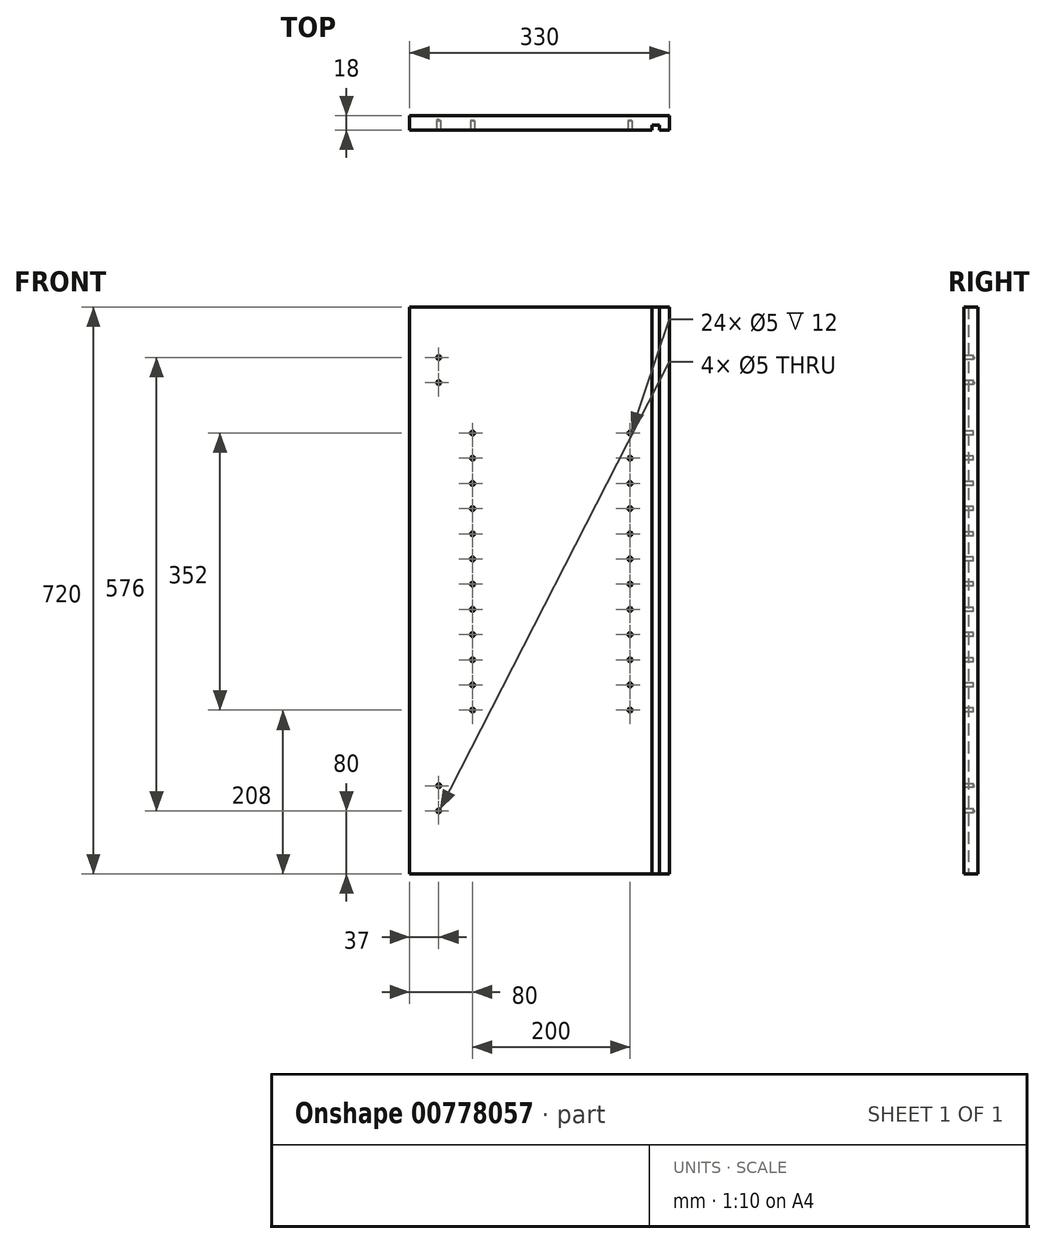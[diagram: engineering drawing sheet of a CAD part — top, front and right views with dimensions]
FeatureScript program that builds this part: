
annotation { "Feature Type Name" : "Feature", "Feature Type Description" : "" }
export const myFeature = defineFeature(function(context is Context, id is Id, definition is map)
    precondition{}
    {
        {
            var Q0;
            Q0=qCreatedBy(makeId("Front.planeOp"),FACE);
            var sketch = newSketch(context, id + "F0", { "sketchPlane" : qUnion([Q0])});
            skLineSegment(sketch, "E0.bottom", {"start": v(243.8, -214.98) * mm, "end": v(305.16, -214.98) * mm});
            skLineSegment(sketch, "E0.top", {"start": v(243.8, -338.54) * mm, "end": v(305.16, -338.54) * mm});
            skLineSegment(sketch, "E0.left", {"start": v(243.8, -214.98) * mm, "end": v(243.8, -338.54) * mm});
            skLineSegment(sketch, "E0.right", {"start": v(305.16, -214.98) * mm, "end": v(305.16, -338.54) * mm});
            skLineSegment(sketch, "E1.bottom", {"start": v(-330, 720) * mm, "end": v(0, 720) * mm});
            skLineSegment(sketch, "E1.top", {"start": v(-330, 0) * mm, "end": v(0, 0) * mm});
            skLineSegment(sketch, "E1.left", {"start": v(-330, 720) * mm, "end": v(-330, 0) * mm});
            skLineSegment(sketch, "E1.right", {"start": v(0, 720) * mm, "end": v(0, 0) * mm});
            skSolve(sketch);
        }
        {
            var Q0;
            Q0=makeQuery(id+"F0.imprint","IMPRINT",FACE,{"disambiguationData":[TD([[makeQuery(id+"F0.imprint","IMPRINT",EDGE,{"derivedFrom":sQuery(id+"F0.wireOp",EDGE,"E1.bottom")}),-1.0]])]});
            extrude(context, id + "F1", {"entities" : qUnion([Q0]), "depth" : 18 * mm, "offsetDistance" : 25 * mm});
        }
        {
            var Q0;
            Q0=makeQuery(id+"F1.opExtrude","CAP_FACE",FACE,{"disambiguationData":[OSD([sQuery(id+"F0.wireOp",EDGE,"E1.bottom"),sQuery(id+"F0.wireOp",EDGE,"E1.top"),sQuery(id+"F0.wireOp",EDGE,"E1.left"),sQuery(id+"F0.wireOp",EDGE,"E1.right")])],"isStart":false});
            var sketch = newSketch(context, id + "F2", { "sketchPlane" : qUnion([Q0])});
            skLineSegment(sketch, "E2", {"start": v(-293, 0) * mm, "end": v(-293, 720) * mm, "construction": true});
            skCircle(sketch, "E3", {"center": v(-293, 656) * mm, "radius": 2.5 * mm});
            skCircle(sketch, "E4", {"center": v(-293, 624) * mm, "radius": 2.5 * mm});
            skCircle(sketch, "E5", {"center": v(-293, 80) * mm, "radius": 2.5 * mm});
            skCircle(sketch, "E6", {"center": v(-293, 112) * mm, "radius": 2.5 * mm});
            skSolve(sketch);
        }
        {
            var Q0;
            Q0=sQuery(id+"F2.wireOp",VERTEX,"E3.center");
            var Q1;
            Q1=sQuery(id+"F2.wireOp",VERTEX,"E4.center");
            var Q2;
            Q2=sQuery(id+"F2.wireOp",VERTEX,"E6.center");
            var Q3;
            Q3=sQuery(id+"F2.wireOp",VERTEX,"E5.center");
            var Q4;
            Q4=makeQuery(id+"F1.opExtrude","SWEPT_BODY",BODY,{"disambiguationData":[OSD([sQuery(id+"F0.wireOp",EDGE,"E1.bottom"),sQuery(id+"F0.wireOp",EDGE,"E1.top"),sQuery(id+"F0.wireOp",EDGE,"E1.left"),sQuery(id+"F0.wireOp",EDGE,"E1.right")])]});
            hole(context, id + "F3", {"style" : HoleStyle.SIMPLE, "endStyle" : HoleEndStyle.BLIND, "holeDiameter" : 5 * mm, "majorDiameter" : 5 * mm, "holeDepth" : 12 * mm, "isTappedThrough" : true, "tappedDepth" : 12 * mm, "tapClearance" : 3, "locations" : qUnion([Q0, Q1, Q2, Q3]), "scope" : qUnion([Q4])});
        }
        {
            var Q0;
            Q0=makeQuery(id+"F1.opExtrude","CAP_FACE",FACE,{"disambiguationData":[OSD([sQuery(id+"F0.wireOp",EDGE,"E1.bottom"),sQuery(id+"F0.wireOp",EDGE,"E1.top"),sQuery(id+"F0.wireOp",EDGE,"E1.left"),sQuery(id+"F0.wireOp",EDGE,"E1.right")])],"isStart":false});
            var sketch = newSketch(context, id + "F4", { "sketchPlane" : qUnion([Q0])});
            skLineSegment(sketch, "E7", {"start": v(-12.5, 720) * mm, "end": v(-12.5, 0) * mm});
            skLineSegment(sketch, "E8", {"start": v(-22, 720) * mm, "end": v(-22, 0) * mm});
            skSolve(sketch);
        }
        {
            var Q0;
            {var subQ0=sQuery(id+"F4.wireOp",EDGE,"E7");Q0=makeQuery(id+"F4.imprint","IMPRINT",FACE,{"disambiguationData":[TD([[makeQuery(id+"F4.imprint","IMPRINT",EDGE,{"derivedFrom":subQ0}),-1.0]])]});}
            extrude(context, id + "F5", {"entities" : qUnion([Q0]), "operationType" : NewBodyOperationType.REMOVE, "oppositeDirection" : true, "depth" : 6 * mm, "offsetDistance" : 25 * mm});
        }
        {
            var Q0;
            {var subQ0=sQuery(id+"F0.wireOp",EDGE,"E1.top");var subQ1=sQuery(id+"F0.wireOp",EDGE,"E1.left");var subQ2=sQuery(id+"F0.wireOp",EDGE,"E1.bottom");Q0=makeQuery(id+"F5.boolean.opBoolean","SPLIT",FACE,{"disambiguationData":[TD([makeQuery(id+"F1.opExtrude","SWEPT_FACE",FACE,{"disambiguationData":[OSD([subQ1])]})])],"derivedFrom":makeQuery(id+"F1.opExtrude","CAP_FACE",FACE,{"disambiguationData":[OSD([subQ2,subQ0,subQ1,sQuery(id+"F0.wireOp",EDGE,"E1.right")])],"isStart":false})});}
            var sketch = newSketch(context, id + "F6", { "sketchPlane" : qUnion([Q0])});
            skLineSegment(sketch, "E9", {"start": v(-250, 720) * mm, "end": v(-250, 0) * mm, "construction": true});
            skLineSegment(sketch, "E10", {"start": v(-50, 720) * mm, "end": v(-50, 0) * mm, "construction": true});
            skCircle(sketch, "E11", {"center": v(-250, 208) * mm, "radius": 2.5 * mm});
            skCircle(sketch, "E12.0.1.0", {"center": v(-250, 240) * mm, "radius": 2.5 * mm});
            skCircle(sketch, "E12.0.2.0", {"center": v(-250, 272) * mm, "radius": 2.5 * mm});
            skCircle(sketch, "E12.0.3.0", {"center": v(-250, 304) * mm, "radius": 2.5 * mm});
            skCircle(sketch, "E12.0.4.0", {"center": v(-250, 336) * mm, "radius": 2.5 * mm});
            skCircle(sketch, "E12.0.5.0", {"center": v(-250, 368) * mm, "radius": 2.5 * mm});
            skCircle(sketch, "E12.0.6.0", {"center": v(-250, 400) * mm, "radius": 2.5 * mm});
            skCircle(sketch, "E12.0.7.0", {"center": v(-250, 432) * mm, "radius": 2.5 * mm});
            skCircle(sketch, "E12.0.8.0", {"center": v(-250, 464) * mm, "radius": 2.5 * mm});
            skCircle(sketch, "E12.0.9.0", {"center": v(-250, 496) * mm, "radius": 2.5 * mm});
            skCircle(sketch, "E12.0.10.0", {"center": v(-250, 528) * mm, "radius": 2.5 * mm});
            skCircle(sketch, "E12.0.11.0", {"center": v(-250, 560) * mm, "radius": 2.5 * mm});
            skCircle(sketch, "E12.1.1.0", {"center": v(-250, 240) * mm, "radius": 2.5 * mm});
            skCircle(sketch, "E12.1.2.0", {"center": v(-250, 272) * mm, "radius": 2.5 * mm});
            skCircle(sketch, "E12.1.3.0", {"center": v(-250, 304) * mm, "radius": 2.5 * mm});
            skCircle(sketch, "E12.1.4.0", {"center": v(-250, 336) * mm, "radius": 2.5 * mm});
            skCircle(sketch, "E12.1.5.0", {"center": v(-250, 368) * mm, "radius": 2.5 * mm});
            skCircle(sketch, "E12.1.6.0", {"center": v(-250, 400) * mm, "radius": 2.5 * mm});
            skCircle(sketch, "E12.1.7.0", {"center": v(-250, 432) * mm, "radius": 2.5 * mm});
            skCircle(sketch, "E12.1.8.0", {"center": v(-250, 464) * mm, "radius": 2.5 * mm});
            skCircle(sketch, "E12.1.9.0", {"center": v(-250, 496) * mm, "radius": 2.5 * mm});
            skCircle(sketch, "E12.1.10.0", {"center": v(-250, 528) * mm, "radius": 2.5 * mm});
            skCircle(sketch, "E12.1.11.0", {"center": v(-250, 560) * mm, "radius": 2.5 * mm});
            skLineSegment(sketch, "E12.direction1", {"start": v(-250, 208) * mm, "end": v(-250, 208) * mm});
            skLineSegment(sketch, "E12.direction2", {"start": v(-250, 208) * mm, "end": v(-250, 240) * mm, "construction": true});
            skCircle(sketch, "E13", {"center": v(-50, 208) * mm, "radius": 2.5 * mm});
            skCircle(sketch, "E14.0.1.0", {"center": v(-50, 240) * mm, "radius": 2.5 * mm});
            skCircle(sketch, "E14.0.2.0", {"center": v(-50, 272) * mm, "radius": 2.5 * mm});
            skCircle(sketch, "E14.0.3.0", {"center": v(-50, 304) * mm, "radius": 2.5 * mm});
            skCircle(sketch, "E14.0.4.0", {"center": v(-50, 336) * mm, "radius": 2.5 * mm});
            skCircle(sketch, "E14.0.5.0", {"center": v(-50, 368) * mm, "radius": 2.5 * mm});
            skCircle(sketch, "E14.0.6.0", {"center": v(-50, 400) * mm, "radius": 2.5 * mm});
            skCircle(sketch, "E14.0.7.0", {"center": v(-50, 432) * mm, "radius": 2.5 * mm});
            skCircle(sketch, "E14.0.8.0", {"center": v(-50, 464) * mm, "radius": 2.5 * mm});
            skCircle(sketch, "E14.0.9.0", {"center": v(-50, 496) * mm, "radius": 2.5 * mm});
            skCircle(sketch, "E14.0.10.0", {"center": v(-50, 528) * mm, "radius": 2.5 * mm});
            skCircle(sketch, "E14.0.11.0", {"center": v(-50, 560) * mm, "radius": 2.5 * mm});
            skCircle(sketch, "E14.1.1.0", {"center": v(-50, 240) * mm, "radius": 2.5 * mm});
            skCircle(sketch, "E14.1.2.0", {"center": v(-50, 272) * mm, "radius": 2.5 * mm});
            skCircle(sketch, "E14.1.3.0", {"center": v(-50, 304) * mm, "radius": 2.5 * mm});
            skCircle(sketch, "E14.1.4.0", {"center": v(-50, 336) * mm, "radius": 2.5 * mm});
            skCircle(sketch, "E14.1.5.0", {"center": v(-50, 368) * mm, "radius": 2.5 * mm});
            skCircle(sketch, "E14.1.6.0", {"center": v(-50, 400) * mm, "radius": 2.5 * mm});
            skCircle(sketch, "E14.1.7.0", {"center": v(-50, 432) * mm, "radius": 2.5 * mm});
            skCircle(sketch, "E14.1.8.0", {"center": v(-50, 464) * mm, "radius": 2.5 * mm});
            skCircle(sketch, "E14.1.9.0", {"center": v(-50, 496) * mm, "radius": 2.5 * mm});
            skCircle(sketch, "E14.1.10.0", {"center": v(-50, 528) * mm, "radius": 2.5 * mm});
            skCircle(sketch, "E14.1.11.0", {"center": v(-50, 560) * mm, "radius": 2.5 * mm});
            skCircle(sketch, "E14.2.1.0", {"center": v(-50, 240) * mm, "radius": 2.5 * mm});
            skCircle(sketch, "E14.2.2.0", {"center": v(-50, 272) * mm, "radius": 2.5 * mm});
            skCircle(sketch, "E14.2.3.0", {"center": v(-50, 304) * mm, "radius": 2.5 * mm});
            skCircle(sketch, "E14.2.4.0", {"center": v(-50, 336) * mm, "radius": 2.5 * mm});
            skCircle(sketch, "E14.2.5.0", {"center": v(-50, 368) * mm, "radius": 2.5 * mm});
            skCircle(sketch, "E14.2.6.0", {"center": v(-50, 400) * mm, "radius": 2.5 * mm});
            skCircle(sketch, "E14.2.7.0", {"center": v(-50, 432) * mm, "radius": 2.5 * mm});
            skCircle(sketch, "E14.2.8.0", {"center": v(-50, 464) * mm, "radius": 2.5 * mm});
            skCircle(sketch, "E14.2.9.0", {"center": v(-50, 496) * mm, "radius": 2.5 * mm});
            skCircle(sketch, "E14.2.10.0", {"center": v(-50, 528) * mm, "radius": 2.5 * mm});
            skCircle(sketch, "E14.2.11.0", {"center": v(-50, 560) * mm, "radius": 2.5 * mm});
            skLineSegment(sketch, "E14.direction1", {"start": v(-50, 208) * mm, "end": v(-50, 208) * mm});
            skLineSegment(sketch, "E14.direction2", {"start": v(-50, 208) * mm, "end": v(-50, 240) * mm, "construction": true});
            skSolve(sketch);
        }
        {
            var Q0;
            Q0 = qSketchRegion(id + "F6", true);
            extrude(context, id + "F7", {"entities" : qUnion([Q0]), "operationType" : NewBodyOperationType.REMOVE, "oppositeDirection" : true, "depth" : 12 * mm, "offsetDistance" : 25 * mm});
        }
    });
